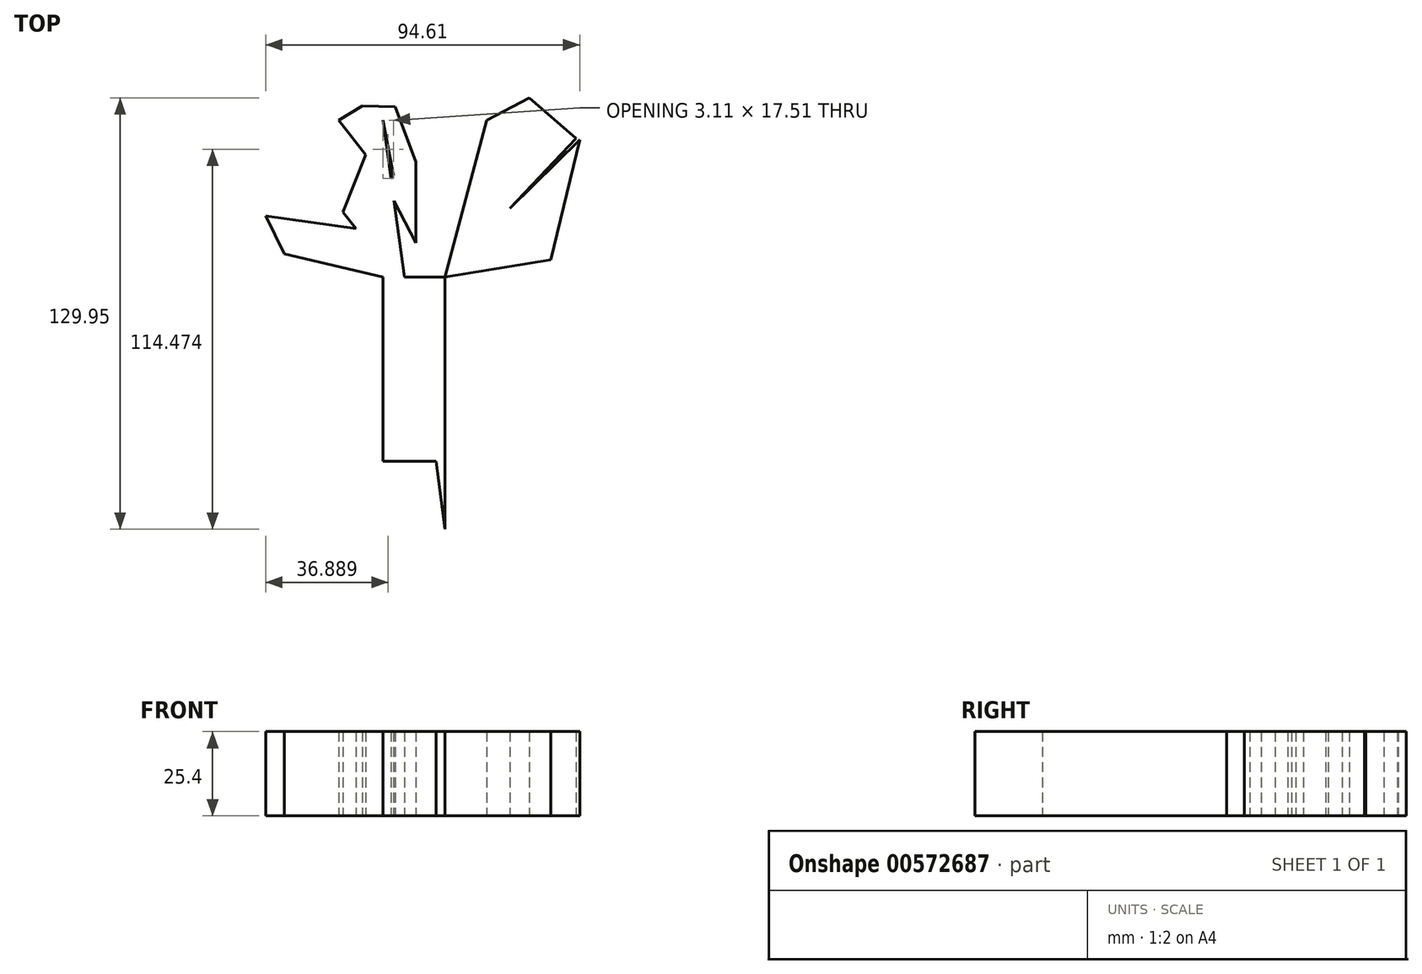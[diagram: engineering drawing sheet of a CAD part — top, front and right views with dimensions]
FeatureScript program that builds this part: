
annotation { "Feature Type Name" : "Feature", "Feature Type Description" : "" }
export const myFeature = defineFeature(function(context is Context, id is Id, definition is map)
    precondition{}
    {
        {
            var Q0;
            Q0=qCreatedBy(makeId("Top.planeOp"),FACE);
            var sketch = newSketch(context, id + "F0", { "sketchPlane" : qUnion([Q0])});
            skLineSegment(sketch, "E0", {"start": v(-9.93, -38.84) * mm, "end": v(8.76, -38.84) * mm});
            skLineSegment(sketch, "E1", {"start": v(8.76, -38.84) * mm, "end": v(8.76, 16.64) * mm});
            skLineSegment(sketch, "E2", {"start": v(8.76, 16.64) * mm, "end": v(28.32, 37.38) * mm});
            skLineSegment(sketch, "E3", {"start": v(28.32, 37.38) * mm, "end": v(40.59, 35.04) * mm});
            skLineSegment(sketch, "E4", {"start": v(40.59, 35.04) * mm, "end": v(28.32, 37.38) * mm});
            skLineSegment(sketch, "E5", {"start": v(28.32, 37.38) * mm, "end": v(48.21, 58.45) * mm});
            skLineSegment(sketch, "E6", {"start": v(48.21, 58.45) * mm, "end": v(18.54, 27.01) * mm});
            skLineSegment(sketch, "E7", {"start": v(18.54, 27.01) * mm, "end": v(21.03, 40.05) * mm});
            skLineSegment(sketch, "E8", {"start": v(21.03, 40.05) * mm, "end": v(18.54, 27.01) * mm});
            skLineSegment(sketch, "E9", {"start": v(38.27, 47.92) * mm, "end": v(38.27, 62.78) * mm});
            skLineSegment(sketch, "E10", {"start": v(38.27, 62.78) * mm, "end": v(38.27, 47.92) * mm});
            skLineSegment(sketch, "E11", {"start": v(8.76, 16.64) * mm, "end": v(21.32, 63.95) * mm});
            skLineSegment(sketch, "E12", {"start": v(21.32, 63.95) * mm, "end": v(34.16, 70.67) * mm});
            skLineSegment(sketch, "E13", {"start": v(34.16, 70.67) * mm, "end": v(21.32, 63.95) * mm});
            skLineSegment(sketch, "E14", {"start": v(18.54, 53.5) * mm, "end": v(31.83, 58.1) * mm});
            skLineSegment(sketch, "E15", {"start": v(31.83, 58.1) * mm, "end": v(18.54, 53.5) * mm});
            skLineSegment(sketch, "E16", {"start": v(15.98, 43.84) * mm, "end": v(10.93, 53.5) * mm});
            skLineSegment(sketch, "E17", {"start": v(10.93, 53.5) * mm, "end": v(15.98, 43.84) * mm});
            skLineSegment(sketch, "E18", {"start": v(13.72, 36.2) * mm, "end": v(1.32, 47.92) * mm});
            skLineSegment(sketch, "E19", {"start": v(1.32, 47.92) * mm, "end": v(13.72, 36.2) * mm});
            skLineSegment(sketch, "E20", {"start": v(-9.93, -38.84) * mm, "end": v(-9.93, 16.64) * mm});
            skLineSegment(sketch, "E21", {"start": v(-9.93, 16.64) * mm, "end": v(8.76, 16.64) * mm});
            skLineSegment(sketch, "E22", {"start": v(0, 16.64) * mm, "end": v(0, 68.62) * mm});
            skLineSegment(sketch, "E23", {"start": v(0, 68.62) * mm, "end": v(0, 56.94) * mm});
            skLineSegment(sketch, "E24", {"start": v(0, 56.94) * mm, "end": v(13.72, 67.45) * mm});
            skLineSegment(sketch, "E25", {"start": v(13.72, 67.45) * mm, "end": v(0, 56.94) * mm});
            skLineSegment(sketch, "E26", {"start": v(0, 27.01) * mm, "end": v(-6.81, 40.05) * mm});
            skLineSegment(sketch, "E27", {"start": v(-6.81, 40.05) * mm, "end": v(0, 27.01) * mm});
            skLineSegment(sketch, "E28", {"start": v(0, 21.9) * mm, "end": v(8.76, 35.04) * mm});
            skLineSegment(sketch, "E29", {"start": v(8.76, 35.04) * mm, "end": v(3.4, 27.01) * mm});
            skLineSegment(sketch, "E30", {"start": v(3.4, 27.01) * mm, "end": v(0, 21.9) * mm});
            skLineSegment(sketch, "E31", {"start": v(0, 40.05) * mm, "end": v(6.13, 53.5) * mm});
            skLineSegment(sketch, "E32", {"start": v(6.13, 53.5) * mm, "end": v(0, 40.05) * mm});
            skLineSegment(sketch, "E33", {"start": v(0, 51.4) * mm, "end": v(-6.81, 69.5) * mm});
            skLineSegment(sketch, "E34", {"start": v(-6.81, 69.5) * mm, "end": v(0, 51.4) * mm});
            skLineSegment(sketch, "E35", {"start": v(-6.81, 16.64) * mm, "end": v(-41.17, 61.03) * mm});
            skLineSegment(sketch, "E36", {"start": v(-41.17, 61.03) * mm, "end": v(-33.71, 51.4) * mm});
            skLineSegment(sketch, "E37", {"start": v(-33.71, 51.4) * mm, "end": v(-30.43, 68.62) * mm});
            skLineSegment(sketch, "E38", {"start": v(-30.43, 68.62) * mm, "end": v(-33.71, 51.4) * mm});
            skLineSegment(sketch, "E39", {"start": v(-30.48, 47.22) * mm, "end": v(-49.35, 51.4) * mm});
            skLineSegment(sketch, "E40", {"start": v(-49.35, 51.4) * mm, "end": v(-30.48, 47.22) * mm});
            skLineSegment(sketch, "E41", {"start": v(-21.96, 36.2) * mm, "end": v(-15.18, 53.5) * mm});
            skLineSegment(sketch, "E42", {"start": v(-15.18, 53.5) * mm, "end": v(-23.27, 63.95) * mm});
            skLineSegment(sketch, "E43", {"start": v(-23.27, 63.95) * mm, "end": v(-15.48, 68.62) * mm});
            skLineSegment(sketch, "E44", {"start": v(-15.48, 68.62) * mm, "end": v(-23.27, 63.95) * mm});
            skLineSegment(sketch, "E45", {"start": v(-18.1, 31.22) * mm, "end": v(-45.26, 35.04) * mm});
            skLineSegment(sketch, "E46", {"start": v(-45.26, 35.04) * mm, "end": v(-18.1, 31.22) * mm});
            skLineSegment(sketch, "E47", {"start": v(-12.26, 23.65) * mm, "end": v(-39.71, 23.65) * mm});
            skLineSegment(sketch, "E48", {"start": v(-39.71, 23.65) * mm, "end": v(-11.68, 23.65) * mm});
            skLineSegment(sketch, "E49", {"start": v(-9.93, 40.05) * mm, "end": v(-11.68, 23.65) * mm});
            skLineSegment(sketch, "E50", {"start": v(-9.93, 16.64) * mm, "end": v(-30.48, 30.35) * mm});
            skLineSegment(sketch, "E51", {"start": v(-30.48, 30.35) * mm, "end": v(-30.48, 40.05) * mm});
            skLineSegment(sketch, "E52", {"start": v(-30.48, 40.05) * mm, "end": v(-30.48, 30.35) * mm});
            skLineSegment(sketch, "E53", {"start": v(-3.5, 16.64) * mm, "end": v(-9.93, 63.95) * mm});
            skLineSegment(sketch, "E54", {"start": v(-9.93, 63.95) * mm, "end": v(-6.81, 47.22) * mm});
            skLineSegment(sketch, "E55", {"start": v(-6.81, 47.22) * mm, "end": v(-16.1, 37.38) * mm});
            skLineSegment(sketch, "E56", {"start": v(-16.1, 37.38) * mm, "end": v(-14.23, 47.22) * mm});
            skLineSegment(sketch, "E57", {"start": v(-9.93, 16.64) * mm, "end": v(-39.71, 23.65) * mm});
            skLineSegment(sketch, "E58", {"start": v(-39.71, 23.65) * mm, "end": v(-45.26, 35.04) * mm});
            skLineSegment(sketch, "E59", {"start": v(-45.26, 35.04) * mm, "end": v(-49.35, 51.4) * mm});
            skLineSegment(sketch, "E60", {"start": v(-49.35, 51.4) * mm, "end": v(-41.17, 61.03) * mm});
            skLineSegment(sketch, "E61", {"start": v(-41.17, 61.03) * mm, "end": v(-30.43, 68.62) * mm});
            skLineSegment(sketch, "E62", {"start": v(-30.43, 68.62) * mm, "end": v(13.72, 67.45) * mm});
            skLineSegment(sketch, "E63", {"start": v(13.72, 67.45) * mm, "end": v(34.16, 70.67) * mm});
            skLineSegment(sketch, "E64", {"start": v(34.16, 70.67) * mm, "end": v(48.21, 58.45) * mm});
            skLineSegment(sketch, "E65", {"start": v(49.35, 58.1) * mm, "end": v(28.32, 37.38) * mm});
            skLineSegment(sketch, "E66", {"start": v(-6.81, -38.84) * mm, "end": v(-23.27, -56.28) * mm});
            skLineSegment(sketch, "E67", {"start": v(-23.27, -56.28) * mm, "end": v(-6.81, -38.84) * mm});
            skLineSegment(sketch, "E68", {"start": v(-4.38, -38.84) * mm, "end": v(-12.26, -58.96) * mm});
            skLineSegment(sketch, "E69", {"start": v(-12.26, -58.96) * mm, "end": v(-4.38, -38.84) * mm});
            skLineSegment(sketch, "E70", {"start": v(-1.17, -38.84) * mm, "end": v(-1.17, -59.28) * mm});
            skLineSegment(sketch, "E71", {"start": v(-1.17, -59.28) * mm, "end": v(-1.17, -38.84) * mm});
            skLineSegment(sketch, "E72", {"start": v(3.4, -38.84) * mm, "end": v(-1.17, -59.28) * mm});
            skLineSegment(sketch, "E73", {"start": v(6.13, -38.84) * mm, "end": v(8.76, -59.28) * mm});
            skLineSegment(sketch, "E74", {"start": v(8.76, -59.28) * mm, "end": v(8.76, -38.84) * mm});
            skLineSegment(sketch, "E75", {"start": v(8.76, 16.64) * mm, "end": v(40.59, 21.9) * mm});
            skLineSegment(sketch, "E76", {"start": v(40.59, 21.9) * mm, "end": v(49.35, 58.1) * mm});
            skLineSegment(sketch, "E77", {"start": v(-9.93, -38.84) * mm, "end": v(-23.27, -56.28) * mm});
            skLineSegment(sketch, "E78", {"start": v(-4.38, -38.84) * mm, "end": v(-7.07, -45.71) * mm});
            skLineSegment(sketch, "E79", {"start": v(-7.07, -45.71) * mm, "end": v(-12.26, -58.96) * mm});
            skSolve(sketch);
        }
        {
            var Q0;
            {var subQ3=sQuery(id+"F0.wireOp",EDGE,"E1");Q0=makeQuery(id+"F0.imprint","IMPRINT",FACE,{"disambiguationData":[TD([[makeQuery(id+"F0.imprint","IMPRINT",EDGE,{"derivedFrom":subQ3}),1.0]])]});}
            var Q1;
            {var subQ0=sQuery(id+"F0.wireOp",EDGE,"E71");Q1=makeQuery(id+"F0.imprint","IMPRINT",FACE,{"disambiguationData":[TD([[makeQuery(id+"F0.imprint","IMPRINT",EDGE,{"derivedFrom":subQ0}),-1.0]])]});}
            var Q2;
            {var subQ2=sQuery(id+"F0.wireOp",EDGE,"E73");Q2=makeQuery(id+"F0.imprint","IMPRINT",FACE,{"disambiguationData":[TD([[makeQuery(id+"F0.imprint","IMPRINT",EDGE,{"derivedFrom":subQ2}),1.0]])]});}
            var Q3;
            {var subQ2=sQuery(id+"F0.wireOp",EDGE,"E2");Q3=makeQuery(id+"F0.imprint","IMPRINT",FACE,{"disambiguationData":[TD([[makeQuery(id+"F0.imprint","IMPRINT",EDGE,{"derivedFrom":subQ2}),-1.0]])]});}
            var Q4;
            {var subQ1=sQuery(id+"F0.wireOp",EDGE,"E2");Q4=makeQuery(id+"F0.imprint","IMPRINT",FACE,{"disambiguationData":[TD([[makeQuery(id+"F0.imprint","IMPRINT",EDGE,{"derivedFrom":subQ1}),1.0]])]});}
            var Q5;
            {var subQ0=sQuery(id+"F0.wireOp",EDGE,"E41");Q5=makeQuery(id+"F0.imprint","IMPRINT",FACE,{"disambiguationData":[TD([[makeQuery(id+"F0.imprint","IMPRINT",EDGE,{"derivedFrom":subQ0}),-1.0]])]});}
            var Q6;
            {var subQ1=sQuery(id+"F0.wireOp",EDGE,"E22");var subQ3=sQuery(id+"F0.wireOp",EDGE,"E34");var subQ4=makeQuery(id+"F0.imprint","INTERSECT",VERTEX,{"derivedFrom":[subQ1,subQ3]});Q6=makeQuery(id+"F0.imprint","IMPRINT",FACE,{"disambiguationData":[TD([[makeQuery(id+"F0.imprint","IMPRINT",EDGE,{"disambiguationData":[TD([[subQ4,1.0]])],"derivedFrom":subQ3}),1.0]])]});}
            var Q7;
            {var subQ0=sQuery(id+"F0.wireOp",EDGE,"E25");Q7=makeQuery(id+"F0.imprint","IMPRINT",FACE,{"disambiguationData":[TD([[makeQuery(id+"F0.imprint","IMPRINT",EDGE,{"derivedFrom":subQ0}),-1.0]])]});}
            var Q8;
            {var subQ0=sQuery(id+"F0.wireOp",EDGE,"E38");Q8=makeQuery(id+"F0.imprint","IMPRINT",FACE,{"disambiguationData":[TD([[makeQuery(id+"F0.imprint","IMPRINT",EDGE,{"derivedFrom":subQ0}),1.0]])]});}
            var Q9;
            Q9=makeQuery(id+"F0.imprint","IMPRINT",FACE,{"disambiguationData":[TD([[makeQuery(id+"F0.imprint","IMPRINT",EDGE,{"derivedFrom":sQuery(id+"F0.wireOp",EDGE,"E36")}),1.0]])]});
            var Q10;
            {var subQ0=sQuery(id+"F0.wireOp",EDGE,"E36");Q10=makeQuery(id+"F0.imprint","IMPRINT",FACE,{"disambiguationData":[TD([[makeQuery(id+"F0.imprint","IMPRINT",EDGE,{"derivedFrom":subQ0}),-1.0]])]});}
            var Q11;
            {var subQ3=sQuery(id+"F0.wireOp",EDGE,"E40");Q11=makeQuery(id+"F0.imprint","IMPRINT",FACE,{"disambiguationData":[TD([[makeQuery(id+"F0.imprint","IMPRINT",EDGE,{"derivedFrom":subQ3}),-1.0]])]});}
            var Q12;
            {var subQ7=sQuery(id+"F0.wireOp",EDGE,"E58");Q12=makeQuery(id+"F0.imprint","IMPRINT",FACE,{"disambiguationData":[TD([[makeQuery(id+"F0.imprint","IMPRINT",EDGE,{"derivedFrom":subQ7}),-1.0]])]});}
            var Q13;
            {var subQ0=sQuery(id+"F0.wireOp",EDGE,"E48");var subQ1=makeQuery(id+"F0.imprint","IMPRINT",VERTEX,{"derivedFrom":subQ0});Q13=makeQuery(id+"F0.imprint","IMPRINT",FACE,{"disambiguationData":[TD([[makeQuery(id+"F0.imprint","IMPRINT",EDGE,{"disambiguationData":[TD([[subQ1,1.0]])],"derivedFrom":subQ0}),-1.0]])]});}
            var Q14;
            {var subQ0=sQuery(id+"F0.wireOp",EDGE,"E57");Q14=makeQuery(id+"F0.imprint","IMPRINT",FACE,{"disambiguationData":[TD([[makeQuery(id+"F0.imprint","IMPRINT",EDGE,{"derivedFrom":subQ0}),-1.0]])]});}
            var Q15;
            {var subQ12=sQuery(id+"F0.wireOp",EDGE,"E13");Q15=makeQuery(id+"F0.imprint","IMPRINT",FACE,{"disambiguationData":[TD([[makeQuery(id+"F0.imprint","IMPRINT",EDGE,{"derivedFrom":subQ12}),-1.0]])]});}
            var Q16;
            {var subQ1=sQuery(id+"F0.wireOp",EDGE,"E22");var subQ5=makeQuery(id+"F0.imprint","IMPRINT",VERTEX,{"disambiguationData":[OD(0.0)],"derivedFrom":subQ1});Q16=makeQuery(id+"F0.imprint","IMPRINT",FACE,{"disambiguationData":[TD([[makeQuery(id+"F0.imprint","IMPRINT",EDGE,{"disambiguationData":[TD([[subQ5,1.0]])],"derivedFrom":subQ1}),1.0]])]});}
            var Q17;
            {var subQ0=sQuery(id+"F0.wireOp",EDGE,"E48");var subQ1=makeQuery(id+"F0.imprint","IMPRINT",VERTEX,{"derivedFrom":subQ0});Q17=makeQuery(id+"F0.imprint","IMPRINT",FACE,{"disambiguationData":[TD([[makeQuery(id+"F0.imprint","IMPRINT",EDGE,{"disambiguationData":[TD([[subQ1,1.0]])],"derivedFrom":subQ0}),1.0]])]});}
            extrude(context, id + "F1", {"entities" : qUnion([Q0, Q1, Q2, Q3, Q4, Q5, Q6, Q7, Q8, Q9, Q10, Q11, Q12, Q13, Q14, Q15, Q16, Q17]), "depth" : 25.4 * mm, "offsetDistance" : 25.4 * mm});
        }
    });
